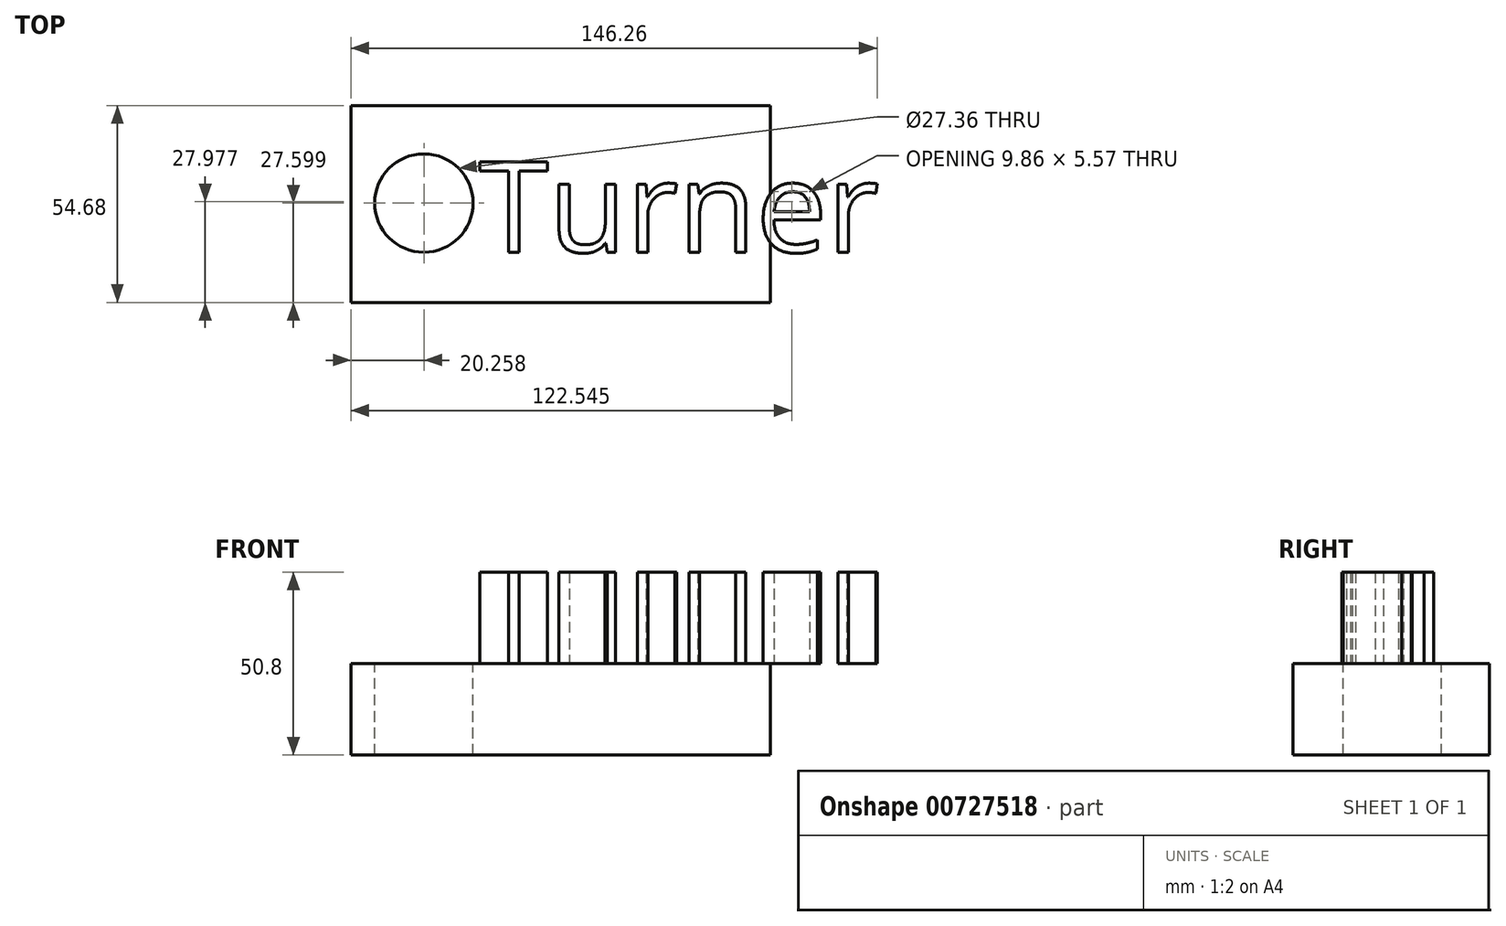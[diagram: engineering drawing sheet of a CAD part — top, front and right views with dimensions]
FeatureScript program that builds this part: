
annotation { "Feature Type Name" : "Feature", "Feature Type Description" : "" }
export const myFeature = defineFeature(function(context is Context, id is Id, definition is map)
    precondition{}
    {
        {
            var Q0;
            Q0=qCreatedBy(makeId("Top.planeOp"),FACE);
            var sketch = newSketch(context, id + "F0", { "sketchPlane" : qUnion([Q0])});
            skLineSegment(sketch, "E0.bottom", {"start": v(-58, 40.72) * mm, "end": v(58.57, 40.72) * mm});
            skLineSegment(sketch, "E0.top", {"start": v(-58, -13.96) * mm, "end": v(58.57, -13.96) * mm});
            skLineSegment(sketch, "E0.left", {"start": v(-58, 40.72) * mm, "end": v(-58, -13.96) * mm});
            skLineSegment(sketch, "E0.right", {"start": v(58.57, 40.72) * mm, "end": v(58.57, -13.96) * mm});
            skSolve(sketch);
        }
        {
            var Q0;
            Q0=makeQuery(id+"F0.imprint","IMPRINT",FACE,{"disambiguationData":[TD([[makeQuery(id+"F0.imprint","IMPRINT",EDGE,{"derivedFrom":sQuery(id+"F0.wireOp",EDGE,"E0.bottom")}),-1.0]])]});
            extrude(context, id + "F1", {"entities" : qUnion([Q0]), "depth" : 25.4 * mm, "offsetDistance" : 25.4 * mm});
        }
        {
            var Q0;
            Q0=makeQuery(id+"F1.opExtrude","CAP_FACE",FACE,{"disambiguationData":[OSD([sQuery(id+"F0.wireOp",EDGE,"E0.bottom"),sQuery(id+"F0.wireOp",EDGE,"E0.top"),sQuery(id+"F0.wireOp",EDGE,"E0.left"),sQuery(id+"F0.wireOp",EDGE,"E0.right")])],"isStart":false});
            var sketch = newSketch(context, id + "F2", { "sketchPlane" : qUnion([Q0])});
            skCircle(sketch, "E1", {"center": v(-37.73, 13.64) * mm, "radius": 13.68 * mm});
            skSolve(sketch);
        }
        {
            var Q0;
            Q0=makeQuery(id+"F2.imprint","IMPRINT",FACE,{"disambiguationData":[TD([[makeQuery(id+"F2.imprint","IMPRINT",EDGE,{"derivedFrom":sQuery(id+"F2.wireOp",EDGE,"E1")}),1.0]])]});
            extrude(context, id + "F3", {"entities" : qUnion([Q0]), "operationType" : NewBodyOperationType.REMOVE, "oppositeDirection" : true, "depth" : 25.4 * mm, "offsetDistance" : 25.4 * mm});
        }
        {
            var Q0;
            Q0=makeQuery(id+"F1.opExtrude","CAP_FACE",FACE,{"disambiguationData":[OSD([sQuery(id+"F0.wireOp",EDGE,"E0.bottom"),sQuery(id+"F0.wireOp",EDGE,"E0.top"),sQuery(id+"F0.wireOp",EDGE,"E0.left"),sQuery(id+"F0.wireOp",EDGE,"E0.right")])],"isStart":false});
            var sketch = newSketch(context, id + "F4", { "sketchPlane" : qUnion([Q0])});
            skText(sketch, "E2", { "text": "Turner", "fontName": "OpenSans-Regular.ttf"});
            const initialGuessF4  = {"E2": [-0.02248, 0, 1, 0, 0.02536]};
            skSetInitialGuess(sketch, initialGuessF4);
            skSolve(sketch);
        }
        {
            var Q0;
            Q0 = qSketchRegion(id + "F4", true);
            extrude(context, id + "F5", {"entities" : qUnion([Q0]), "operationType" : NewBodyOperationType.ADD, "depth" : 25.4 * mm, "offsetDistance" : 25.4 * mm});
        }
    });
